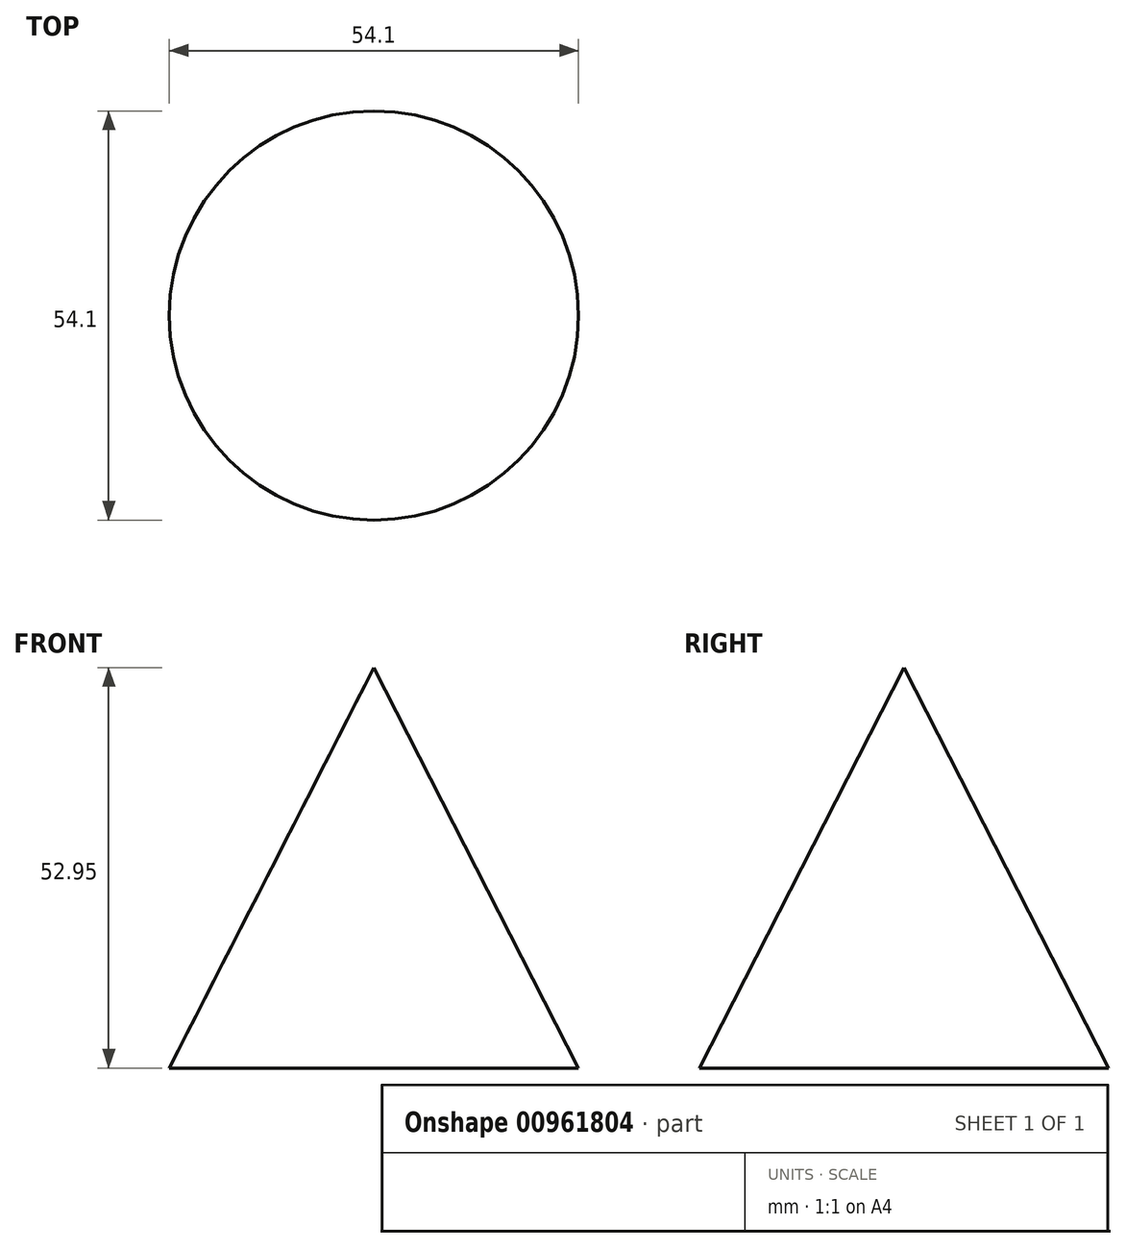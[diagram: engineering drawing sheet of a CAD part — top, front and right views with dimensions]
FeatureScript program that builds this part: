
annotation { "Feature Type Name" : "Feature", "Feature Type Description" : "" }
export const myFeature = defineFeature(function(context is Context, id is Id, definition is map)
    precondition{}
    {
        {
            var Q0;
            Q0=qCreatedBy(makeId("Front.planeOp"),FACE);
            var sketch = newSketch(context, id + "F0", { "sketchPlane" : qUnion([Q0])});
            skLineSegment(sketch, "E0", {"start": v(0, 0) * mm, "end": v(0, 52.95) * mm});
            skLineSegment(sketch, "E1", {"start": v(0, 52.95) * mm, "end": v(27.05, 0) * mm});
            skLineSegment(sketch, "E2", {"start": v(27.05, 0) * mm, "end": v(0, 0) * mm});
            skLineSegment(sketch, "E3", {"start": v(27.05, 0) * mm, "end": v(33.6, 0) * mm});
            skSolve(sketch);
        }
        {
            var Q0;
            Q0 = qSketchRegion(id + "F0", true);
            var Q1;
            Q1=sQuery(id+"F0.wireOp",EDGE,"E0");
            revolve(context, id + "F1", {"surfaceOperationType" : NewSurfaceOperationType.NEW, "entities" : qUnion([Q0]), "axis" : qUnion([Q1]), "revolveType" : RevolveType.FULL});
        }
    });
